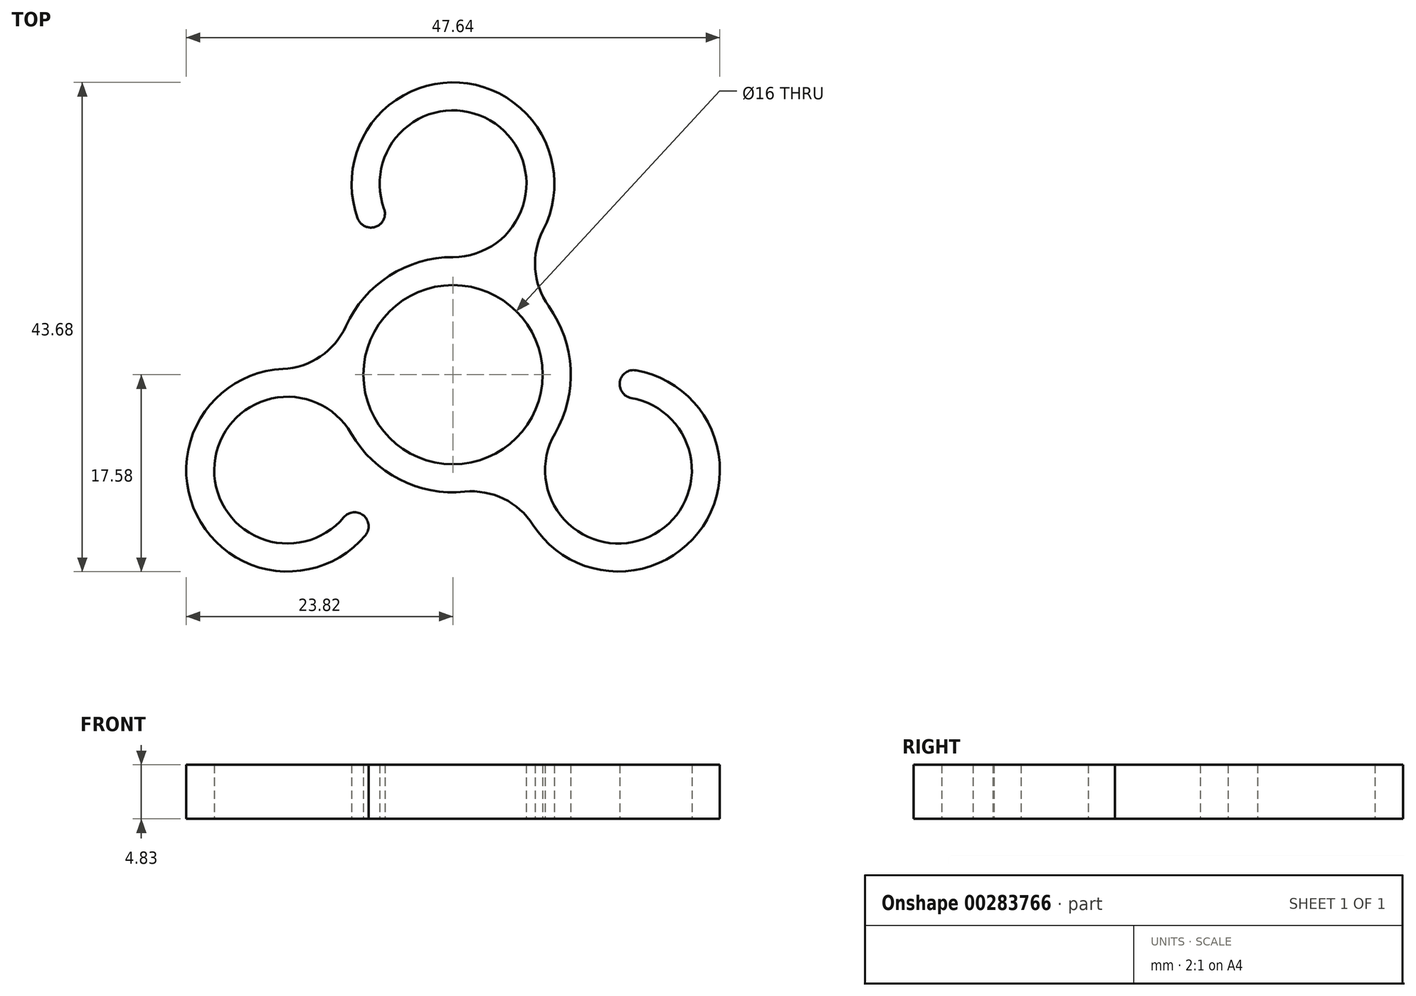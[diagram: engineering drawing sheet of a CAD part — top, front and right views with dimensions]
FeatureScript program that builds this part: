
annotation { "Feature Type Name" : "Feature", "Feature Type Description" : "" }
export const myFeature = defineFeature(function(context is Context, id is Id, definition is map)
    precondition{}
    {
        {
            var Q0;
            Q0=qCreatedBy(makeId("Top.planeOp"),FACE);
            var sketch = newSketch(context, id + "F0", { "sketchPlane" : qUnion([Q0])});
            skCircle(sketch, "E0", {"center": v(0, 0) * mm, "radius": 8 * mm});
            skArc(sketch, "E1", {"start": v(0, 10.5) * mm, "mid": v(-5.7, 8.82) * mm, "end": v(-9.57, 4.33) * mm});
            skArc(sketch, "E2", {"start": v(0, 10.5) * mm, "mid": v(3.76, 22.42) * mm, "end": v(-6.15, 14.8) * mm});
            skArc(sketch, "E3", {"start": v(8.04, 12.9) * mm, "mid": v(0.58, 26.08) * mm, "end": v(-8.5, 13.95) * mm});
            skLineSegment(sketch, "E4", {"start": v(-6.15, 14.8) * mm, "end": v(-8.5, 13.95) * mm, "construction": true});
            skArc(sketch, "E5", {"start": v(-8.5, 13.95) * mm, "mid": v(-6.9, 13.2) * mm, "end": v(-6.15, 14.8) * mm});
            skPoint(sketch, "E6.visualSharp", {"position": v(4.77, 9.36) * mm});
            skArc(sketch, "E6.filletArc", {"start": v(8.04, 12.9) * mm, "mid": v(7.33, 9.44) * mm, "end": v(8.53, 6.12) * mm});
            skArc(sketch, "E7.1.0", {"start": v(-15.19, 0.52) * mm, "mid": v(-11.84, 1.63) * mm, "end": v(-9.57, 4.33) * mm});
            skArc(sketch, "E7.1.1", {"start": v(-9.1, -5.25) * mm, "mid": v(-21.3, -7.95) * mm, "end": v(-9.75, -12.74) * mm});
            skArc(sketch, "E7.1.2", {"start": v(-7.83, -14.34) * mm, "mid": v(-7.99, -12.58) * mm, "end": v(-9.75, -12.74) * mm});
            skPoint(sketch, "E7.1.3", {"position": v(-10.49, -0.55) * mm});
            skArc(sketch, "E7.1.4", {"start": v(-15.19, 0.52) * mm, "mid": v(-22.88, -12.54) * mm, "end": v(-7.83, -14.34) * mm});
            skLineSegment(sketch, "E7.1.5", {"start": v(-9.75, -12.74) * mm, "end": v(-7.83, -14.34) * mm, "construction": true});
            skArc(sketch, "E7.2.0", {"start": v(7.15, -13.4) * mm, "mid": v(4.5, -11.07) * mm, "end": v(1.03, -10.45) * mm});
            skArc(sketch, "E7.2.1", {"start": v(9.1, -5.25) * mm, "mid": v(17.53, -14.46) * mm, "end": v(15.9, -2.07) * mm});
            skArc(sketch, "E7.2.2", {"start": v(16.34, 0.39) * mm, "mid": v(14.89, -0.63) * mm, "end": v(15.9, -2.07) * mm});
            skPoint(sketch, "E7.2.3", {"position": v(5.72, -8.8) * mm});
            skArc(sketch, "E7.2.4", {"start": v(7.15, -13.4) * mm, "mid": v(22.3, -13.54) * mm, "end": v(16.34, 0.39) * mm});
            skLineSegment(sketch, "E7.2.5", {"start": v(15.9, -2.07) * mm, "end": v(16.34, 0.39) * mm, "construction": true});
            skArc(sketch, "E8.trimOffspring", {"start": v(-9.1, -5.25) * mm, "mid": v(-4.8, -9.34) * mm, "end": v(1.03, -10.45) * mm});
            skArc(sketch, "E9.trimOffspring", {"start": v(9.1, -5.25) * mm, "mid": v(10.49, 0.52) * mm, "end": v(8.53, 6.12) * mm});
            skSolve(sketch);
        }
        {
            var Q0;
            Q0 = qSketchRegion(id + "F0", true);
            extrude(context, id + "F1", {"entities" : qUnion([Q0]), "depth" : 4.83 * mm, "offsetDistance" : 25 * mm});
        }
    });
